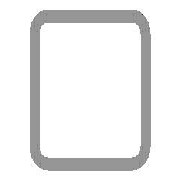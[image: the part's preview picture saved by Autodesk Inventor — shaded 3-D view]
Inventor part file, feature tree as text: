
AUTODESK INVENTOR PART (.ipt)
format: ipt  version: 2018 (Build 220112000, 112)  size: 130,048 bytes
history: native  units: mm (DEFAULTED — no unit token found)
features: other x3, sketch x3, extrude x1, plane x1
ambient origin geometry x8: Origin, YZ Plane, XZ Plane, XY Plane, X Axis, Y Axis, Z Axis, Center Point
bodies: Solid1 (feature_tree)
feature tree (8):
  other  "Driven Length"
  other  "Piano iniziale"
  other  "Piano finale"
  extrude  "Corpo"  TaperAngle=0.0deg  [1 undecoded]
  sketch  "Schizzo"
  sketch  "Sketch3"  dims[d3=230.0mm d4=0.0mm]
  plane  "Work Plane3"
  sketch  "Sketch4"  dims[d7=4.0mm d9=40.0mm d11=40.0mm d12=2.0mm d13=-0.0mm d14=230.0mm d15=20.0mm d16=20.0mm d17=90.0deg d18=230.0mm]
note: 1 required parameter value undecoded (feature->parameter linkage not recoverable at this tier; creation-order binding heuristic only, values carry confidence <= 0.55)
